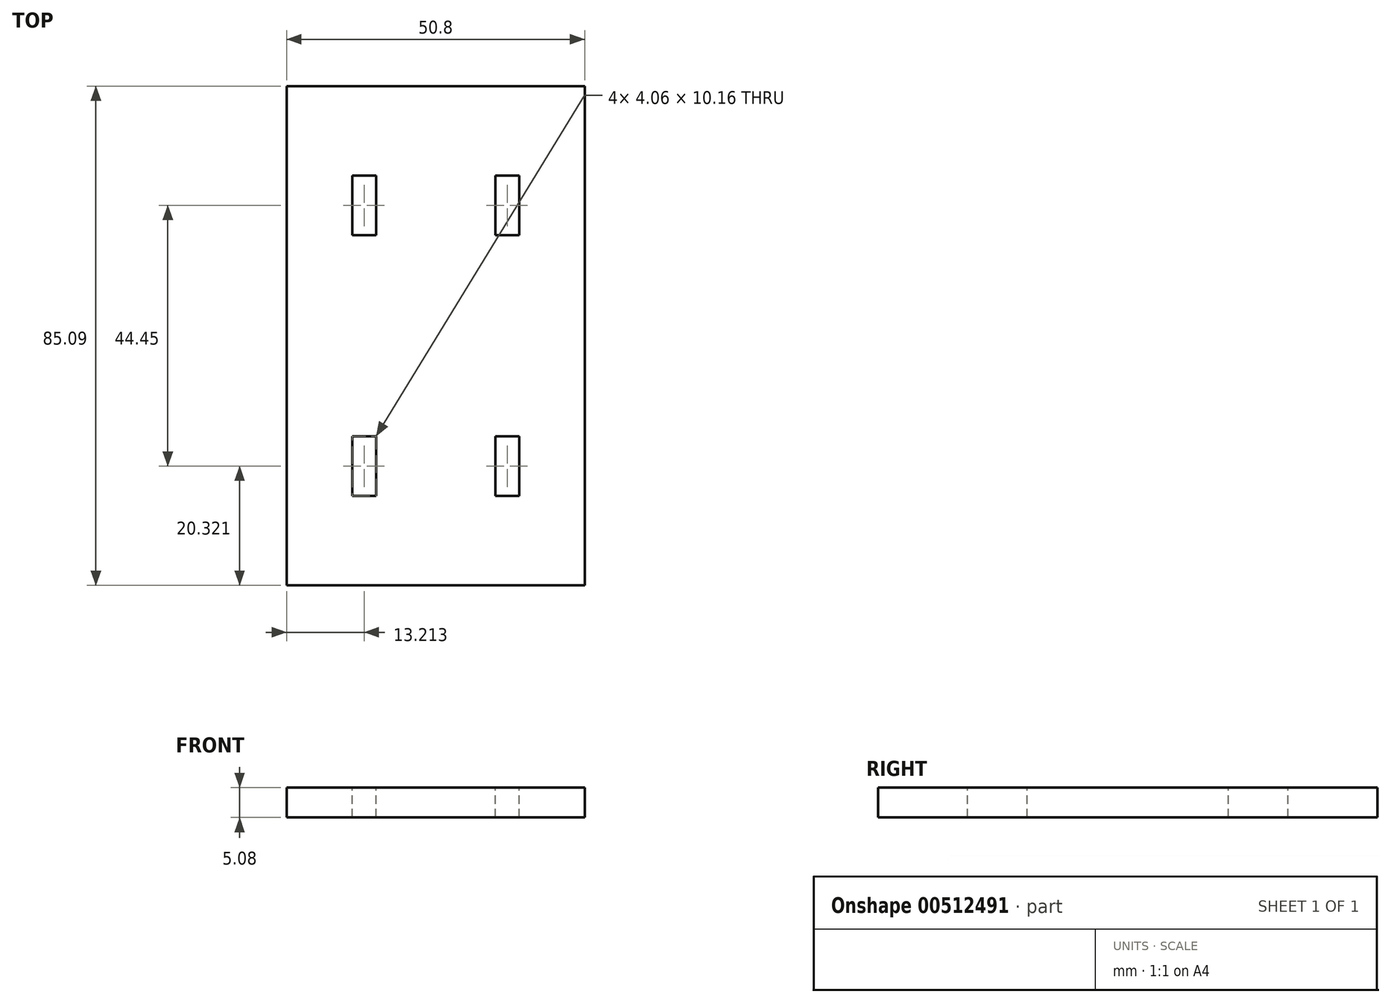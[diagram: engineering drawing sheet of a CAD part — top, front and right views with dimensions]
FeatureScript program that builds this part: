
annotation { "Feature Type Name" : "Feature", "Feature Type Description" : "" }
export const myFeature = defineFeature(function(context is Context, id is Id, definition is map)
    precondition{}
    {
        {
            var Q0;
            Q0=qCreatedBy(makeId("Top.planeOp"),FACE);
            var sketch = newSketch(context, id + "F0", { "sketchPlane" : qUnion([Q0])});
            skLineSegment(sketch, "E0.bottom", {"start": v(-21.7, 66.83) * mm, "end": v(29.1, 66.83) * mm});
            skLineSegment(sketch, "E0.top", {"start": v(-21.7, -18.26) * mm, "end": v(29.1, -18.26) * mm});
            skLineSegment(sketch, "E0.left", {"start": v(-21.7, 66.83) * mm, "end": v(-21.7, -18.26) * mm});
            skLineSegment(sketch, "E0.right", {"start": v(29.1, 66.83) * mm, "end": v(29.1, -18.26) * mm});
            skSolve(sketch);
        }
        {
            var Q0;
            Q0=qSketchRegion(id+"F0",true);
            var Q1;
            Q1=makeQuery(id+"F0.imprint","IMPRINT",FACE,{"disambiguationData":[TD([[makeQuery(id+"F0.imprint","IMPRINT",EDGE,{"derivedFrom":sQuery(id+"F0.wireOp",EDGE,"E0.bottom")}),-1.0]])]});
            extrude(context, id + "F1", {"entities" : qUnion([Q0, Q1]), "depth" : 5.08 * mm});
        }
        {
            var Q0;
            Q0=makeQuery(id+"F1.opExtrude","CAP_FACE",FACE,{"disambiguationData":[OSD([sQuery(id+"F0.wireOp",EDGE,"E0.bottom"),sQuery(id+"F0.wireOp",EDGE,"E0.top"),sQuery(id+"F0.wireOp",EDGE,"E0.left"),sQuery(id+"F0.wireOp",EDGE,"E0.right")])],"isStart":false});
            var sketch = newSketch(context, id + "F2", { "sketchPlane" : qUnion([Q0])});
            skLineSegment(sketch, "E1.bottom", {"start": v(-10.52, 51.6) * mm, "end": v(-6.46, 51.6) * mm});
            skLineSegment(sketch, "E1.top", {"start": v(-10.52, 41.43) * mm, "end": v(-6.46, 41.43) * mm});
            skLineSegment(sketch, "E1.left", {"start": v(-10.52, 51.6) * mm, "end": v(-10.52, 41.43) * mm});
            skLineSegment(sketch, "E1.right", {"start": v(-6.46, 51.6) * mm, "end": v(-6.46, 41.43) * mm});
            skLineSegment(sketch, "E2.bottom", {"start": v(13.86, 51.6) * mm, "end": v(17.93, 51.6) * mm});
            skLineSegment(sketch, "E2.top", {"start": v(13.86, 41.43) * mm, "end": v(17.93, 41.43) * mm});
            skLineSegment(sketch, "E2.left", {"start": v(13.86, 51.6) * mm, "end": v(13.86, 41.43) * mm});
            skLineSegment(sketch, "E2.right", {"start": v(17.93, 51.6) * mm, "end": v(17.93, 41.43) * mm});
            skLineSegment(sketch, "E3.bottom", {"start": v(-6.46, 7.14) * mm, "end": v(-10.52, 7.14) * mm});
            skLineSegment(sketch, "E3.top", {"start": v(-6.46, -3.02) * mm, "end": v(-10.52, -3.02) * mm});
            skLineSegment(sketch, "E3.left", {"start": v(-6.46, 7.14) * mm, "end": v(-6.46, -3.02) * mm});
            skLineSegment(sketch, "E3.right", {"start": v(-10.52, 7.14) * mm, "end": v(-10.52, -3.02) * mm});
            skLineSegment(sketch, "E4.bottom", {"start": v(13.86, 7.14) * mm, "end": v(17.93, 7.14) * mm});
            skLineSegment(sketch, "E4.top", {"start": v(13.86, -3.02) * mm, "end": v(17.93, -3.02) * mm});
            skLineSegment(sketch, "E4.left", {"start": v(13.86, 7.14) * mm, "end": v(13.86, -3.02) * mm});
            skLineSegment(sketch, "E4.right", {"start": v(17.93, 7.14) * mm, "end": v(17.93, -3.02) * mm});
            skLineSegment(sketch, "E5", {"start": v(3.7, 66.83) * mm, "end": v(3.7, -18.26) * mm, "construction": true});
            skSolve(sketch);
        }
        {
            var Q0;
            Q0=makeQuery(id+"F2.imprint","IMPRINT",FACE,{"disambiguationData":[TD([[makeQuery(id+"F2.imprint","IMPRINT",EDGE,{"derivedFrom":sQuery(id+"F2.wireOp",EDGE,"E1.bottom")}),-1.0]])]});
            var Q1;
            Q1=makeQuery(id+"F2.imprint","IMPRINT",FACE,{"disambiguationData":[TD([[makeQuery(id+"F2.imprint","IMPRINT",EDGE,{"derivedFrom":sQuery(id+"F2.wireOp",EDGE,"E2.bottom")}),-1.0]])]});
            var Q2;
            Q2=makeQuery(id+"F2.imprint","IMPRINT",FACE,{"disambiguationData":[TD([[makeQuery(id+"F2.imprint","IMPRINT",EDGE,{"derivedFrom":sQuery(id+"F2.wireOp",EDGE,"E3.bottom")}),1.0]])]});
            var Q3;
            Q3=makeQuery(id+"F2.imprint","IMPRINT",FACE,{"disambiguationData":[TD([[makeQuery(id+"F2.imprint","IMPRINT",EDGE,{"derivedFrom":sQuery(id+"F2.wireOp",EDGE,"E4.bottom")}),-1.0]])]});
            extrude(context, id + "F3", {"entities" : qUnion([Q0, Q1, Q2, Q3]), "operationType" : NewBodyOperationType.REMOVE, "oppositeDirection" : true, "depth" : 25.4 * mm});
        }
    });
